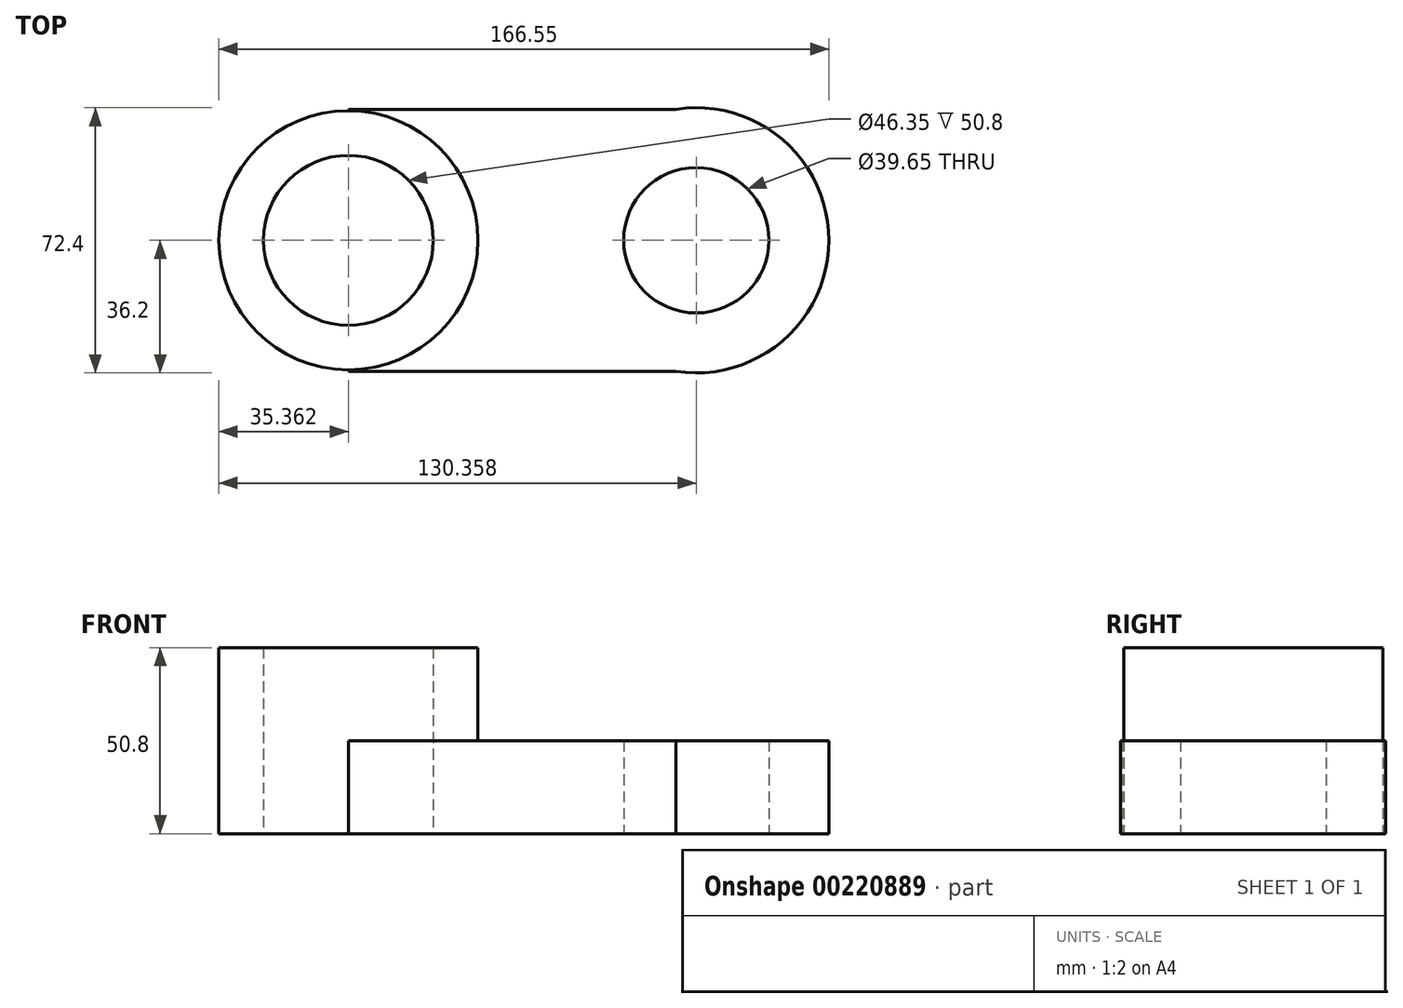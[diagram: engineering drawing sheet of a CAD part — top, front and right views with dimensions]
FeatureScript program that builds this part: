
annotation { "Feature Type Name" : "Feature", "Feature Type Description" : "" }
export const myFeature = defineFeature(function(context is Context, id is Id, definition is map)
    precondition{}
    {
        {
            var Q0;
            Q0=qCreatedBy(makeId("Top.planeOp"),FACE);
            var sketch = newSketch(context, id + "F0", { "sketchPlane" : qUnion([Q0])});
            skLineSegment(sketch, "E0.bottom", {"start": v(-47.5, 35.77) * mm, "end": v(47.5, 35.77) * mm});
            skLineSegment(sketch, "E0.top", {"start": v(-47.5, -35.77) * mm, "end": v(47.5, -35.77) * mm});
            skLineSegment(sketch, "E0.left", {"start": v(-47.5, 35.77) * mm, "end": v(-47.5, 35.36) * mm});
            skPoint(sketch, "E0.middle", {"position": v(0, 0) * mm});
            skCircle(sketch, "E1", {"center": v(-47.5, 0) * mm, "radius": 35.36 * mm});
            skCircle(sketch, "E2", {"center": v(-47.5, 0) * mm, "radius": 23.18 * mm});
            skArc(sketch, "E3", {"start": v(41.96, -35.77) * mm, "mid": v(83.7, 0) * mm, "end": v(41.96, 35.77) * mm});
            skCircle(sketch, "E4", {"center": v(47.5, 0) * mm, "radius": 19.83 * mm});
            skLineSegment(sketch, "E5.trimOffspring", {"start": v(-47.5, -35.36) * mm, "end": v(-47.5, -35.77) * mm});
            skSolve(sketch);
        }
        {
            var Q0;
            Q0=makeQuery(id+"F0.imprint","IMPRINT",FACE,{"disambiguationData":[TD([[makeQuery(id+"F0.imprint","IMPRINT",EDGE,{"derivedFrom":sQuery(id+"F0.wireOp",EDGE,"E2")}),-1.0]])]});
            extrude(context, id + "F1", {"entities" : qUnion([Q0]), "depth" : 50.8 * mm});
        }
        {
            var Q0;
            {var subQ1=sQuery(id+"F0.wireOp",EDGE,"E0.left");Q0=makeQuery(id+"F0.imprint","IMPRINT",FACE,{"disambiguationData":[TD([[makeQuery(id+"F0.imprint","IMPRINT",EDGE,{"derivedFrom":subQ1}),1.0]])]});}
            extrude(context, id + "F2", {"entities" : qUnion([Q0]), "operationType" : NewBodyOperationType.ADD, "depth" : 25.4 * mm});
        }
    });
